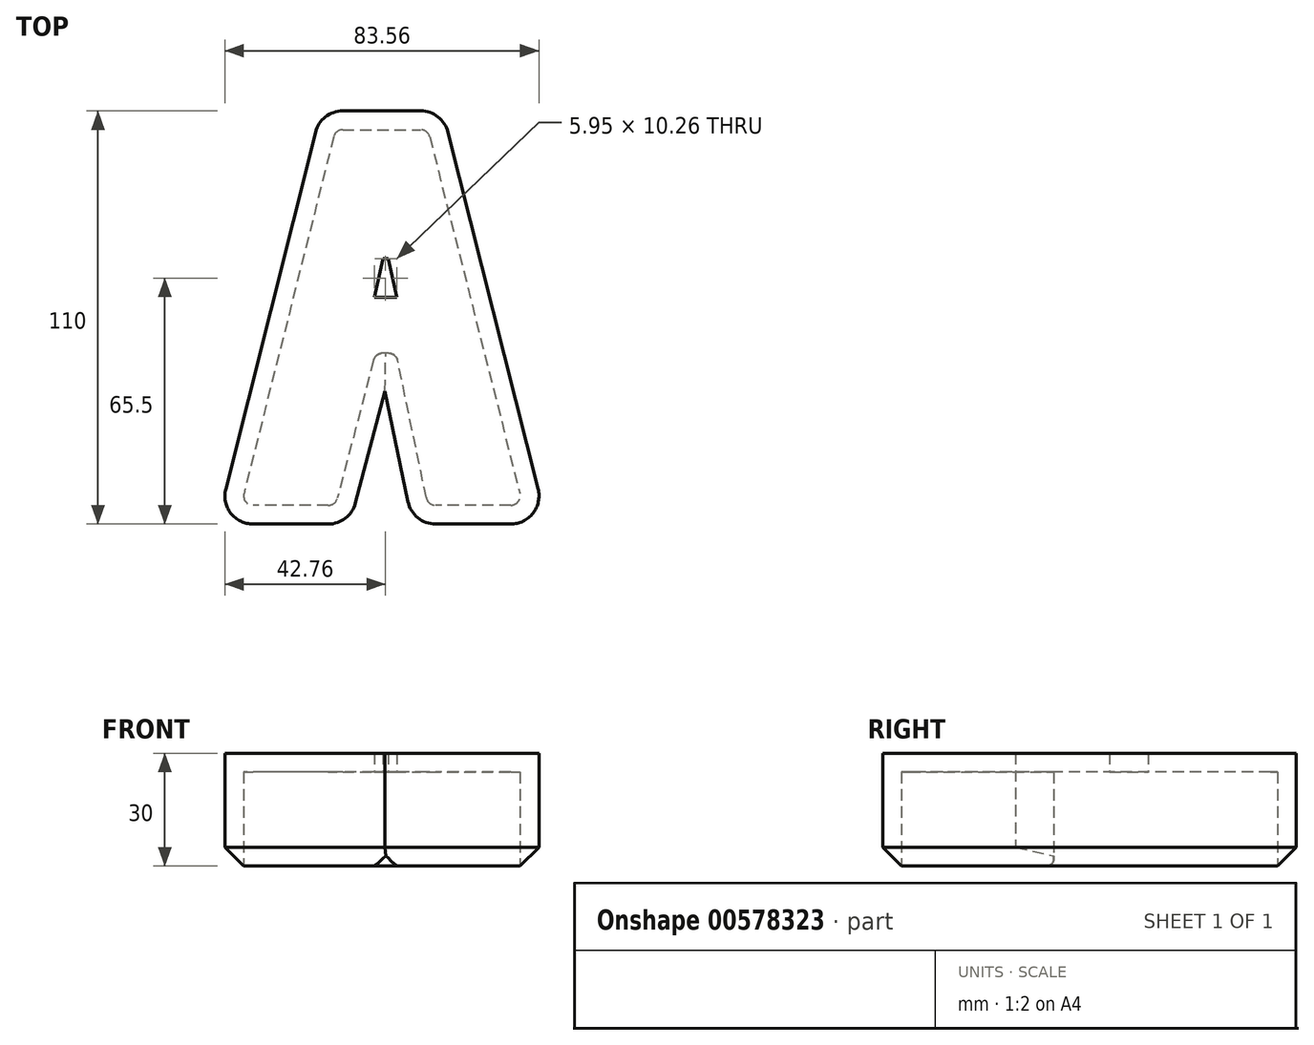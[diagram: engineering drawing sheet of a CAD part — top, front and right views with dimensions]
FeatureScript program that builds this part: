
annotation { "Feature Type Name" : "Feature", "Feature Type Description" : "" }
export const myFeature = defineFeature(function(context is Context, id is Id, definition is map)
    precondition{}
    {
        {
            var Q0;
            Q0=qCreatedBy(makeId("Top.planeOp"),FACE);
            var sketch = newSketch(context, id + "F0", { "sketchPlane" : qUnion([Q0]), "disableImprinting" : false});
            skLineSegment(sketch, "E0", {"start": v(11.75, 57.84) * mm, "end": v(35.73, -37.16) * mm});
            skLineSegment(sketch, "E1", {"start": v(33.3, -40.27) * mm, "end": v(13.3, -40.27) * mm});
            skLineSegment(sketch, "E2", {"start": v(10.85, -38.28) * mm, "end": v(3.22, -1.76) * mm});
            skLineSegment(sketch, "E3", {"start": v(0.77, 0.23) * mm, "end": v(-0.77, 0.23) * mm});
            skLineSegment(sketch, "E4", {"start": v(-3.19, -1.64) * mm, "end": v(-12.84, -38.4) * mm});
            skLineSegment(sketch, "E5", {"start": v(-15.26, -40.27) * mm, "end": v(-35.26, -40.27) * mm});
            skLineSegment(sketch, "E6", {"start": v(-13.8, 57.84) * mm, "end": v(-37.68, -37.16) * mm});
            skLineSegment(sketch, "E7", {"start": v(-11.38, 59.73) * mm, "end": v(9.32, 59.73) * mm});
            skPoint(sketch, "E8.visualSharp", {"position": v(-38.46, -40.27) * mm});
            skArc(sketch, "E8.filletArc", {"start": v(-37.68, -37.16) * mm, "mid": v(-37.23, -39.31) * mm, "end": v(-35.26, -40.27) * mm});
            skPoint(sketch, "E9.visualSharp", {"position": v(-13.33, 59.73) * mm});
            skArc(sketch, "E9.filletArc", {"start": v(-11.38, 59.73) * mm, "mid": v(-12.92, 59.2) * mm, "end": v(-13.8, 57.84) * mm});
            skPoint(sketch, "E10.visualSharp", {"position": v(11.27, 59.73) * mm});
            skArc(sketch, "E10.filletArc", {"start": v(11.75, 57.84) * mm, "mid": v(10.86, 59.2) * mm, "end": v(9.32, 59.73) * mm});
            skPoint(sketch, "E11.visualSharp", {"position": v(11.27, -40.27) * mm});
            skArc(sketch, "E11.filletArc", {"start": v(10.85, -38.28) * mm, "mid": v(11.72, -39.71) * mm, "end": v(13.3, -40.27) * mm});
            skPoint(sketch, "E12.visualSharp", {"position": v(36.51, -40.27) * mm});
            skArc(sketch, "E12.filletArc", {"start": v(33.3, -40.27) * mm, "mid": v(35.27, -39.3) * mm, "end": v(35.73, -37.16) * mm});
            skPoint(sketch, "E13.visualSharp", {"position": v(2.8, 0.23) * mm});
            skArc(sketch, "E13.filletArc", {"start": v(3.22, -1.76) * mm, "mid": v(2.35, -0.33) * mm, "end": v(0.77, 0.23) * mm});
            skPoint(sketch, "E14.visualSharp", {"position": v(-2.7, 0.23) * mm});
            skArc(sketch, "E14.filletArc", {"start": v(-0.77, 0.23) * mm, "mid": v(-2.3, -0.3) * mm, "end": v(-3.19, -1.64) * mm});
            skPoint(sketch, "E15.visualSharp", {"position": v(-13.33, -40.27) * mm});
            skArc(sketch, "E15.filletArc", {"start": v(-15.26, -40.27) * mm, "mid": v(-13.73, -39.75) * mm, "end": v(-12.84, -38.4) * mm});
            skLineSegment(sketch, "E16", {"start": v(-2.98, 15.1) * mm, "end": v(2.98, 15.1) * mm});
            skPoint(sketch, "E17", {"position": v(0, 0.23) * mm});
            skPoint(sketch, "E18", {"position": v(0, 0) * mm});
            skPoint(sketch, "E19", {"position": v(0, 15.1) * mm});
            skLineSegment(sketch, "E20", {"start": v(-2.98, 15.1) * mm, "end": v(-0.66, 25.36) * mm});
            skLineSegment(sketch, "E21", {"start": v(0.66, 25.36) * mm, "end": v(2.98, 15.1) * mm});
            skLineSegment(sketch, "E22", {"start": v(-0.66, 25.36) * mm, "end": v(0.66, 25.36) * mm});
            skArc(sketch, "E23.0", {"start": v(-11.38, 64.73) * mm, "mid": v(-16, 63.14) * mm, "end": v(-18.65, 59.05) * mm});
            skLineSegment(sketch, "E23.1", {"start": v(-11.38, 64.73) * mm, "end": v(9.32, 64.73) * mm});
            skLineSegment(sketch, "E23.2", {"start": v(-0.19, -9.9) * mm, "end": v(-8, -39.68) * mm});
            skArc(sketch, "E23.3", {"start": v(-15.26, -45.27) * mm, "mid": v(-10.68, -43.71) * mm, "end": v(-8, -39.68) * mm});
            skLineSegment(sketch, "E23.4", {"start": v(-15.26, -45.27) * mm, "end": v(-35.26, -45.27) * mm});
            skArc(sketch, "E23.5", {"start": v(-42.53, -35.95) * mm, "mid": v(-41.17, -42.39) * mm, "end": v(-35.26, -45.27) * mm});
            skLineSegment(sketch, "E23.6", {"start": v(5.96, -39.3) * mm, "end": v(-0.19, -9.9) * mm});
            skArc(sketch, "E23.7", {"start": v(5.96, -39.3) * mm, "mid": v(8.57, -43.6) * mm, "end": v(13.3, -45.27) * mm});
            skLineSegment(sketch, "E23.8", {"start": v(-18.65, 59.05) * mm, "end": v(-42.53, -35.95) * mm});
            skLineSegment(sketch, "E23.9", {"start": v(33.3, -45.27) * mm, "end": v(13.3, -45.27) * mm});
            skArc(sketch, "E23.10", {"start": v(33.3, -45.27) * mm, "mid": v(39.22, -42.38) * mm, "end": v(40.57, -35.94) * mm});
            skLineSegment(sketch, "E23.11", {"start": v(16.6, 59.06) * mm, "end": v(40.57, -35.94) * mm});
            skArc(sketch, "E23.12", {"start": v(16.6, 59.06) * mm, "mid": v(13.93, 63.14) * mm, "end": v(9.32, 64.73) * mm});
            skSolve(sketch);
        }
        {
            var Q0;
            Q0 = qSketchRegion(id + "F0", true);
            extrude(context, id + "F1", {"entities" : qUnion([Q0]), "depth" : 30 * mm, "offsetDistance" : 25 * mm});
        }
        {
            var Q0;
            Q0=sQuery(id+"F0.wireOp",EDGE,"E21");
            var Q1;
            Q1=sQuery(id+"F0.wireOp",EDGE,"E16");
            var Q2;
            Q2=sQuery(id+"F0.wireOp",EDGE,"E20");
            var Q3;
            Q3=sQuery(id+"F0.wireOp",EDGE,"E22");
            extrude(context, id + "F2", {"bodyType" : ToolBodyType.SURFACE, "surfaceEntities" : qUnion([Q0, Q1, Q2, Q3]), "depth" : 30 * mm, "offsetDistance" : 25 * mm});
        }
        {
            var Q0;
            Q0=makeQuery(id+"F0.imprint","IMPRINT",FACE,{"disambiguationData":[TD([[makeQuery(id+"F0.imprint","IMPRINT",EDGE,{"derivedFrom":sQuery(id+"F0.wireOp",EDGE,"E0")}),-1.0]])]});
            extrude(context, id + "F3", {"entities" : qUnion([Q0]), "operationType" : NewBodyOperationType.ADD, "depth" : 30 * mm, "offsetDistance" : 25 * mm});
        }
        {
            var Q0;
            Q0=makeQuery(id+"F0.imprint","IMPRINT",FACE,{"disambiguationData":[TD([[makeQuery(id+"F0.imprint","IMPRINT",EDGE,{"derivedFrom":sQuery(id+"F0.wireOp",EDGE,"E0")}),-1.0]])]});
            extrude(context, id + "F4", {"entities" : qUnion([Q0]), "operationType" : NewBodyOperationType.REMOVE, "oppositeDirection" : true, "depth" : -25 * mm, "offsetDistance" : 25 * mm});
        }
        {
            var Q0;
            Q0=makeQuery(id+"F1.opExtrude","CAP_EDGE",EDGE,{"disambiguationData":[OSD([sQuery(id+"F0.wireOp",EDGE,"E23.8")])],"isStart":true});
            chamfer(context, id + "F5", {"entities" : qUnion([Q0]), "chamferType" : ChamferType.OFFSET_ANGLE, "width" : 5 * mm, "oppositeDirection" : false, "angle" : 45 * degree, "tangentPropagation" : true});
        }
    });
